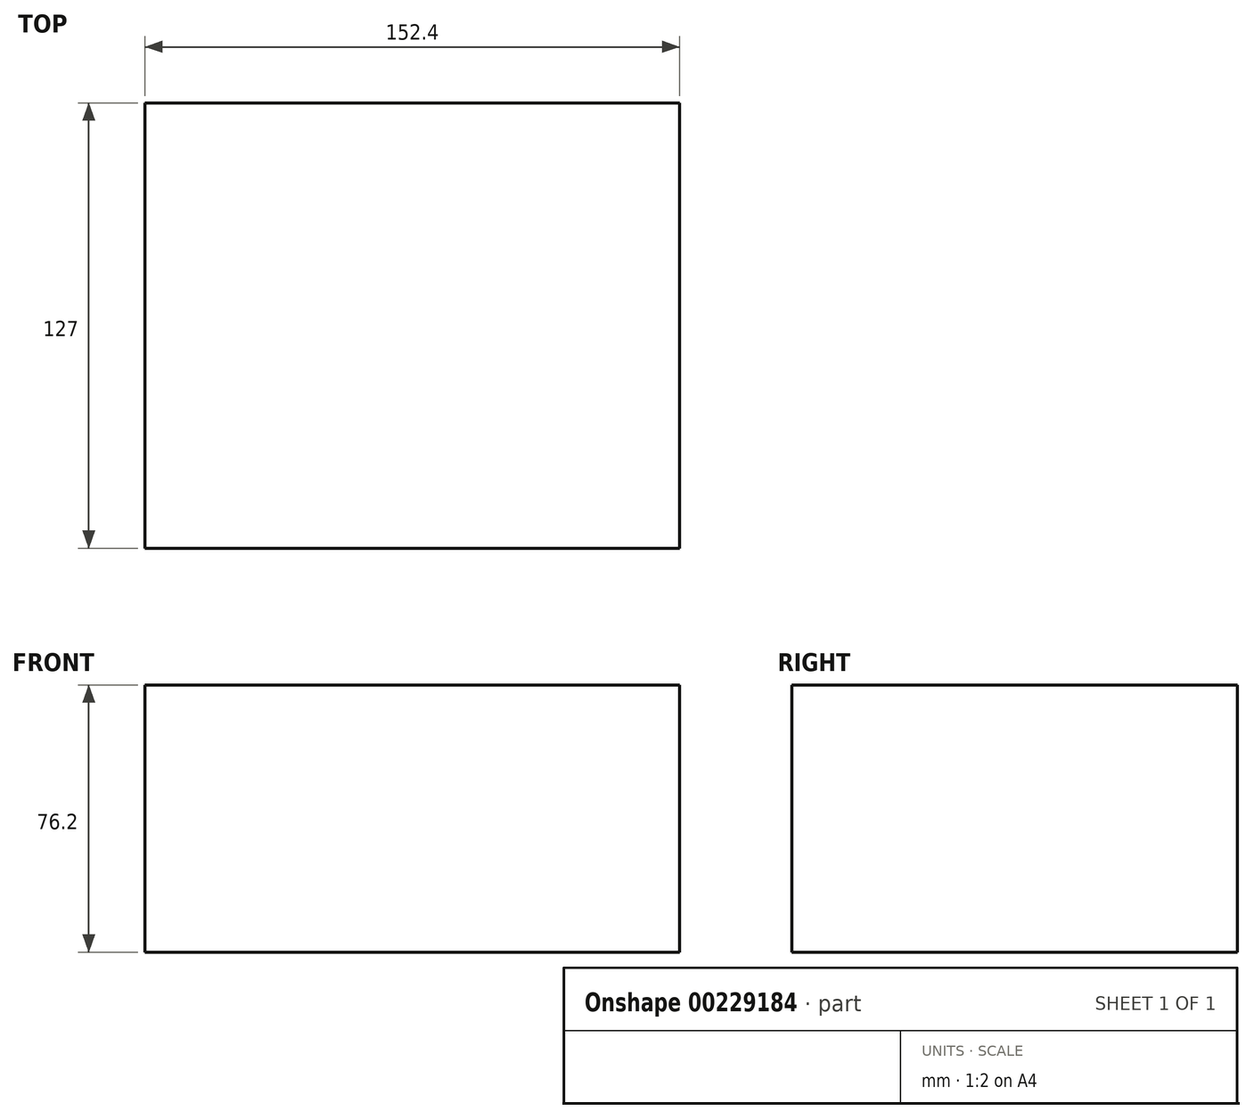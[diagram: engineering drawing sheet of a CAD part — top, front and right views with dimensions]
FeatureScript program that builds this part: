
annotation { "Feature Type Name" : "Feature", "Feature Type Description" : "" }
export const myFeature = defineFeature(function(context is Context, id is Id, definition is map)
    precondition{}
    {
        {
            var Q0;
            Q0=qCreatedBy(makeId("Front.planeOp"),FACE);
            var sketch = newSketch(context, id + "F0", { "sketchPlane" : qUnion([Q0])});
            skLineSegment(sketch, "E0", {"start": v(-76.2, 38.1) * mm, "end": v(76.2, 38.1) * mm});
            skLineSegment(sketch, "E1", {"start": v(76.2, 38.1) * mm, "end": v(76.2, -38.1) * mm});
            skLineSegment(sketch, "E2", {"start": v(76.2, -38.1) * mm, "end": v(-76.2, -38.1) * mm});
            skLineSegment(sketch, "E3", {"start": v(-76.2, -38.1) * mm, "end": v(-76.2, 38.1) * mm});
            skSolve(sketch);
        }
        {
            var Q0;
            Q0 = qSketchRegion(id + "F0", true);
            extrude(context, id + "F1", {"entities" : qUnion([Q0]), "endBound" : BoundingType.SYMMETRIC, "depth" : 127 * mm});
        }
    });
